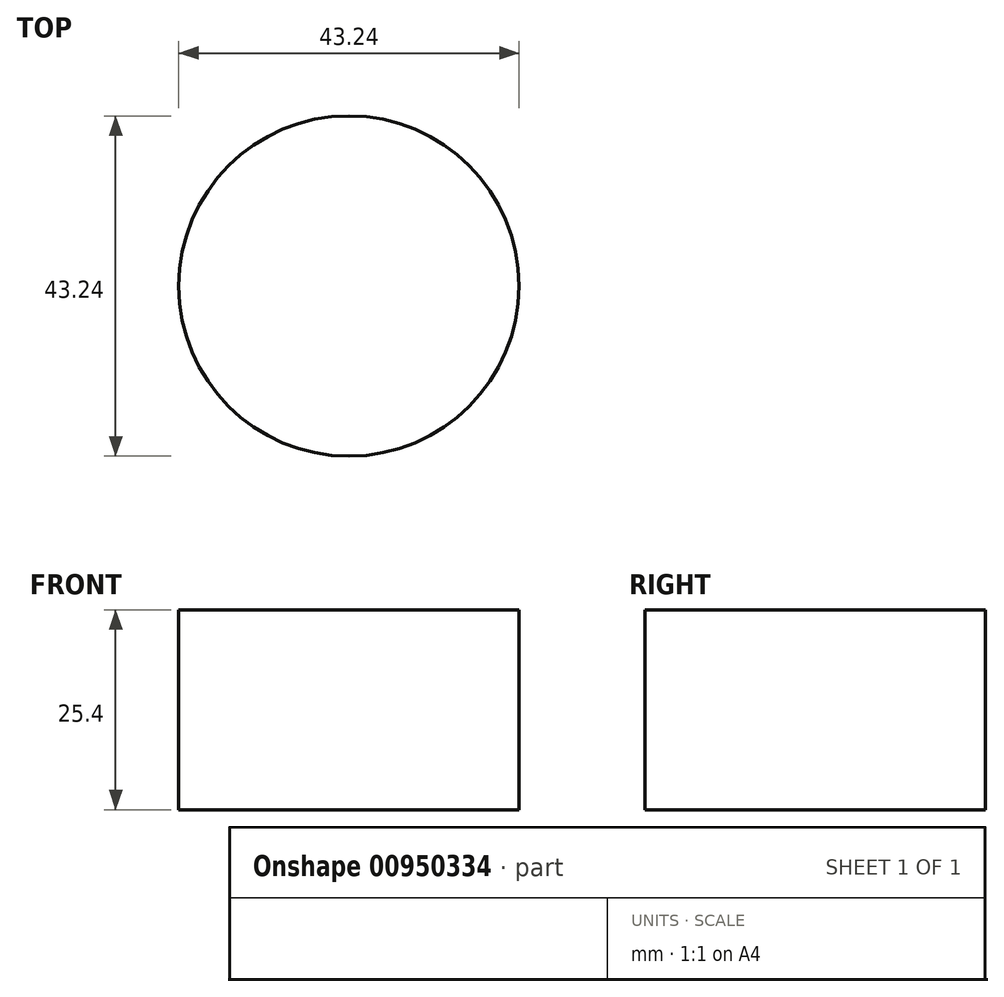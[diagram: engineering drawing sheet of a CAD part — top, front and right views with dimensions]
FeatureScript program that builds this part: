
annotation { "Feature Type Name" : "Feature", "Feature Type Description" : "" }
export const myFeature = defineFeature(function(context is Context, id is Id, definition is map)
    precondition{}
    {
        {
            var Q0;
            Q0=qCreatedBy(makeId("Top.planeOp"),FACE);
            var sketch = newSketch(context, id + "F0", { "sketchPlane" : qUnion([Q0])});
            skCircle(sketch, "E0", {"center": v(0, 0) * mm, "radius": 21.62 * mm});
            skSolve(sketch);
        }
        {
            var Q0;
            Q0=makeQuery(id+"F0.imprint","IMPRINT",FACE,{"disambiguationData":[TD([[makeQuery(id+"F0.imprint","IMPRINT",EDGE,{"derivedFrom":sQuery(id+"F0.wireOp",EDGE,"E0")}),1.0]])]});
            extrude(context, id + "F1", {"entities" : qUnion([Q0]), "depth" : 25.4 * mm, "offsetDistance" : 25.4 * mm});
        }
    });
